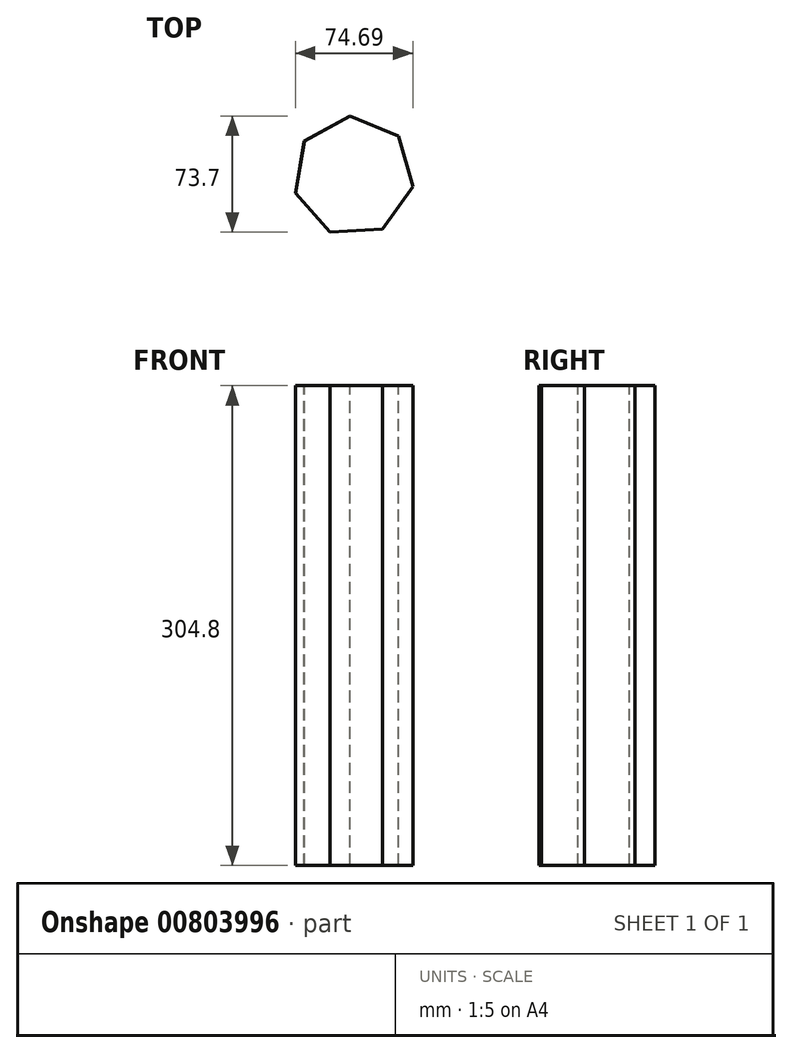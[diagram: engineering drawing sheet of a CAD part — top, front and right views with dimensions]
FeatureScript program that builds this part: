
annotation { "Feature Type Name" : "Feature", "Feature Type Description" : "" }
export const myFeature = defineFeature(function(context is Context, id is Id, definition is map)
    precondition{}
    {
        {
            var Q0;
            Q0=qCreatedBy(makeId("Top.planeOp"),FACE);
            var sketch = newSketch(context, id + "F0", { "sketchPlane" : qUnion([Q0])});
            skCircle(sketch, "E0.cCircle", {"center": v(-7.55, -36.88) * mm, "radius": 34.56 * mm, "construction": true});
            skLineSegment(sketch, "E0.0", {"start": v(-38.76, -14.59) * mm, "end": v(-9.58, 1.42) * mm});
            skLineSegment(sketch, "E0.1", {"start": v(-9.58, 1.42) * mm, "end": v(21.13, -11.4) * mm});
            skLineSegment(sketch, "E0.2", {"start": v(21.13, -11.4) * mm, "end": v(30.25, -43.42) * mm});
            skLineSegment(sketch, "E0.3", {"start": v(30.25, -43.42) * mm, "end": v(10.9, -70.51) * mm});
            skLineSegment(sketch, "E0.4", {"start": v(10.9, -70.51) * mm, "end": v(-22.33, -72.28) * mm});
            skLineSegment(sketch, "E0.5", {"start": v(-22.33, -72.28) * mm, "end": v(-44.44, -47.39) * mm});
            skLineSegment(sketch, "E0.6", {"start": v(-44.44, -47.39) * mm, "end": v(-38.76, -14.59) * mm});
            skPoint(sketch, "E0.0.midPoint", {"position": v(-24.17, -6.58) * mm});
            skSolve(sketch);
        }
        {
            var Q0;
            Q0 = qSketchRegion(id + "F0", true);
            extrude(context, id + "F1", {"entities" : qUnion([Q0]), "oppositeDirection" : true, "depth" : 304.8 * mm, "offsetDistance" : 25.4 * mm});
        }
        {
            var Q0;
            Q0=makeQuery(id+"F1.opExtrude","CAP_FACE",FACE,{"disambiguationData":[OSD([sQuery(id+"F0.wireOp",EDGE,"E0.0"),sQuery(id+"F0.wireOp",EDGE,"E0.1"),sQuery(id+"F0.wireOp",EDGE,"E0.2"),sQuery(id+"F0.wireOp",EDGE,"E0.3"),sQuery(id+"F0.wireOp",EDGE,"E0.4"),sQuery(id+"F0.wireOp",EDGE,"E0.5"),sQuery(id+"F0.wireOp",EDGE,"E0.6")])],"isStart":true});
            shell(context, id + "F2", {"entities" : qUnion([Q0]), "thickness" : 2 / 127 * mm});
        }
    });
